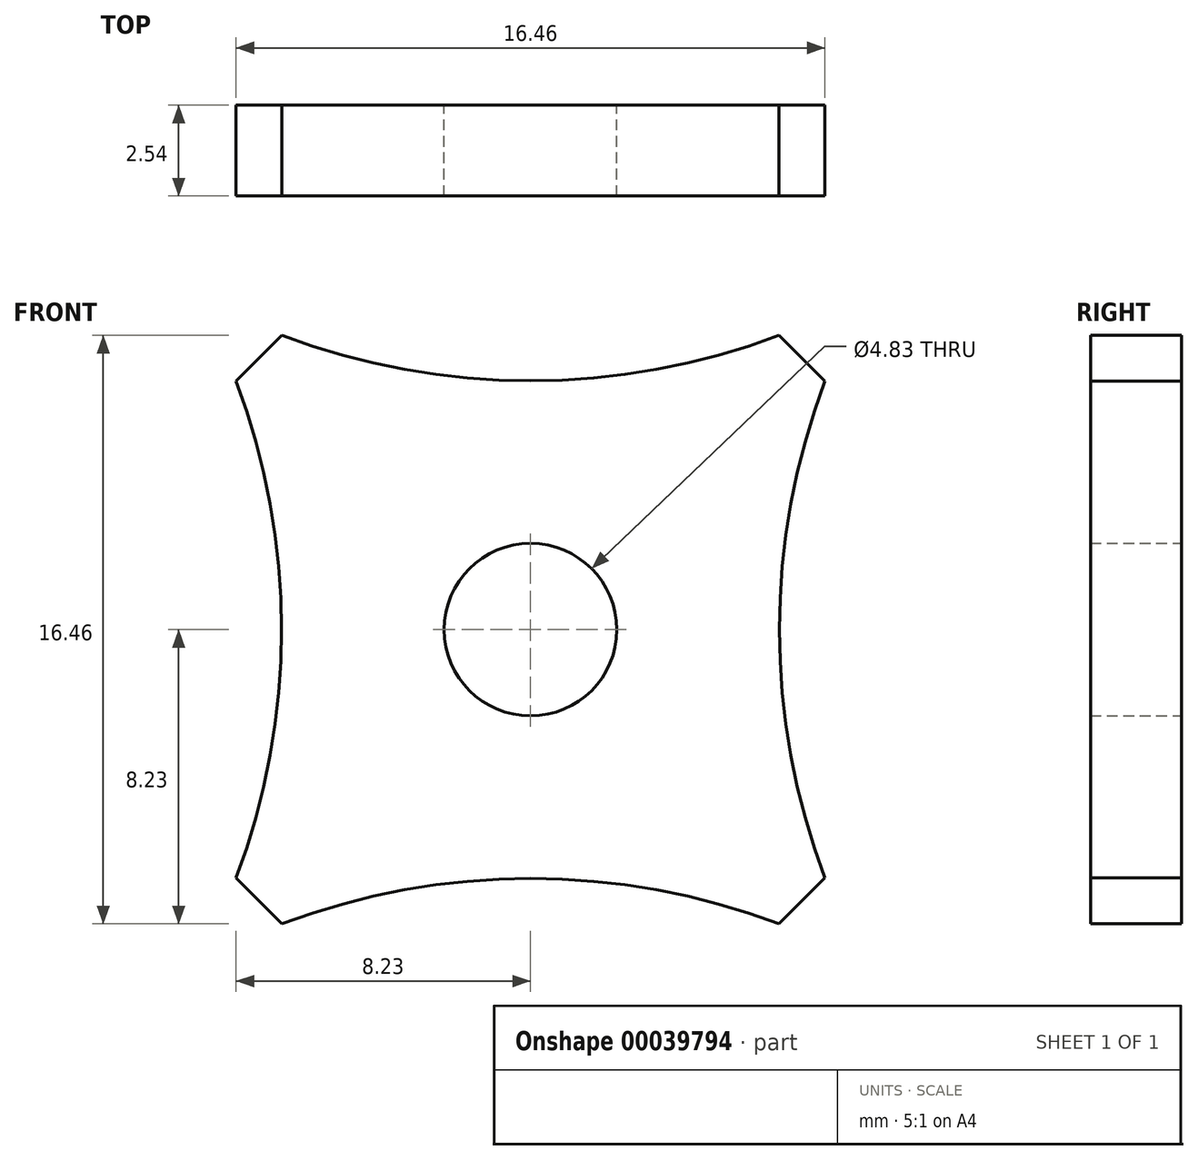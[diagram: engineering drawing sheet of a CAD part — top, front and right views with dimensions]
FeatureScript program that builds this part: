
annotation { "Feature Type Name" : "Feature", "Feature Type Description" : "" }
export const myFeature = defineFeature(function(context is Context, id is Id, definition is map)
    precondition{}
    {
        {
            var Q0;
            Q0=qCreatedBy(makeId("Front.planeOp"),FACE);
            var sketch = newSketch(context, id + "F0", { "sketchPlane" : qUnion([Q0])});
            skCircle(sketch, "E0", {"center": v(0, 0) * mm, "radius": 10.77 * mm, "construction": true});
            skLineSegment(sketch, "E1", {"start": v(0, 0) * mm, "end": v(2.41, 0) * mm});
            skCircle(sketch, "E2", {"center": v(0, 0) * mm, "radius": 2.41 * mm});
            skLineSegment(sketch, "E3", {"start": v(0, 0) * mm, "end": v(-2.41, 0) * mm});
            skLineSegment(sketch, "E4", {"start": v(0, 10.77) * mm, "end": v(0, 0) * mm});
            skLineSegment(sketch, "E5", {"start": v(0, 0) * mm, "end": v(0, -10.77) * mm});
            skLineSegment(sketch, "E6", {"start": v(10.77, 0) * mm, "end": v(8.23, 0) * mm});
            skLineSegment(sketch, "E7", {"start": v(0, 10.77) * mm, "end": v(0, 8.23) * mm});
            skLineSegment(sketch, "E8", {"start": v(-10.77, 0) * mm, "end": v(-8.23, 0) * mm});
            skLineSegment(sketch, "E9", {"start": v(0, -10.77) * mm, "end": v(0, -8.23) * mm});
            skLineSegment(sketch, "E10", {"start": v(-8.23, 0) * mm, "end": v(-8.23, 6.95) * mm, "construction": true});
            skLineSegment(sketch, "E11", {"start": v(-8.23, 6.95) * mm, "end": v(-8.23, -6.95) * mm, "construction": true});
            skLineSegment(sketch, "E12", {"start": v(0, -8.23) * mm, "end": v(-6.95, -8.23) * mm, "construction": true});
            skLineSegment(sketch, "E13", {"start": v(0, -8.23) * mm, "end": v(6.95, -8.23) * mm, "construction": true});
            skLineSegment(sketch, "E14", {"start": v(8.23, 0) * mm, "end": v(8.23, -6.95) * mm, "construction": true});
            skLineSegment(sketch, "E15", {"start": v(8.23, -6.95) * mm, "end": v(8.23, 6.95) * mm, "construction": true});
            skLineSegment(sketch, "E16", {"start": v(0, 8.23) * mm, "end": v(6.95, 8.23) * mm, "construction": true});
            skLineSegment(sketch, "E17", {"start": v(6.95, 8.23) * mm, "end": v(-6.95, 8.23) * mm, "construction": true});
            skLineSegment(sketch, "E18", {"start": v(0, 8.23) * mm, "end": v(0, 6.96) * mm});
            skLineSegment(sketch, "E19", {"start": v(8.23, 0) * mm, "end": v(6.96, 0) * mm});
            skLineSegment(sketch, "E20", {"start": v(-8.23, 0) * mm, "end": v(-6.96, 0) * mm});
            skLineSegment(sketch, "E21", {"start": v(0, -8.23) * mm, "end": v(0, -6.96) * mm});
            skLineSegment(sketch, "E22", {"start": v(6.96, 0) * mm, "end": v(7.6, 0) * mm});
            skArc(sketch, "E23", {"start": v(-8.23, -6.95) * mm, "mid": v(-6.96, 0) * mm, "end": v(-8.23, 6.95) * mm});
            skArc(sketch, "E24", {"start": v(6.95, -8.23) * mm, "mid": v(0, -6.96) * mm, "end": v(-6.95, -8.23) * mm});
            skArc(sketch, "E25", {"start": v(8.23, 6.95) * mm, "mid": v(6.96, 0) * mm, "end": v(8.23, -6.95) * mm});
            skArc(sketch, "E26", {"start": v(-6.95, 8.23) * mm, "mid": v(0, 6.96) * mm, "end": v(6.95, 8.23) * mm});
            skLineSegment(sketch, "E27", {"start": v(-8.23, 6.95) * mm, "end": v(-6.95, 8.23) * mm});
            skLineSegment(sketch, "E28", {"start": v(-8.23, -6.95) * mm, "end": v(-6.95, -8.23) * mm});
            skLineSegment(sketch, "E29", {"start": v(8.23, -6.95) * mm, "end": v(6.95, -8.23) * mm});
            skLineSegment(sketch, "E30", {"start": v(6.95, 8.23) * mm, "end": v(8.23, 6.95) * mm});
            skLineSegment(sketch, "E31", {"start": v(-7.59, 7.59) * mm, "end": v(-7.62, 7.62) * mm});
            skSolve(sketch);
        }
        {
            var Q0;
            Q0 = qSketchRegion(id + "F0", true);
            extrude(context, id + "F1", {"entities" : qUnion([Q0]), "depth" : 2.54 * mm});
        }
    });
